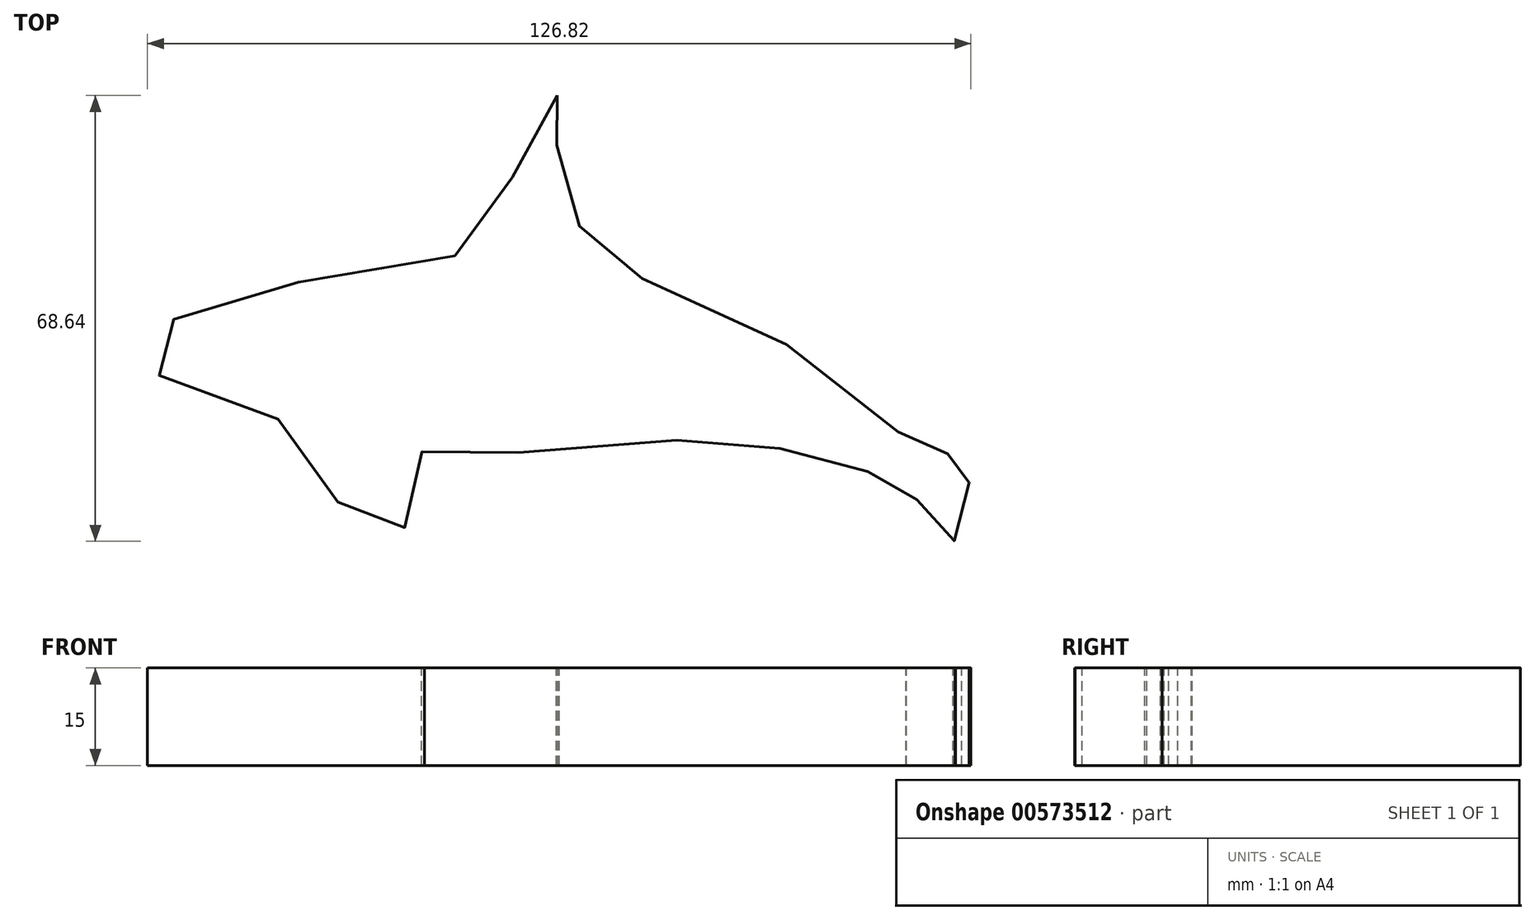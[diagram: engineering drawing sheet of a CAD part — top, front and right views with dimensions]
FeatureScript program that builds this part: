
annotation { "Feature Type Name" : "Feature", "Feature Type Description" : "" }
export const myFeature = defineFeature(function(context is Context, id is Id, definition is map)
    precondition{}
    {
        {
            var Q0;
            Q0=qCreatedBy(makeId("Top.planeOp"),FACE);
            var sketch = newSketch(context, id + "F0", { "sketchPlane" : qUnion([Q0])});
            skFitSpline(sketch, "E0", {"points": [v(3.98, 39.05) * mm, v(4.31, 38.75) * mm, v(4.31, 38.29) * mm, v(4.31, 37.62) * mm, v(4.31, 36.89) * mm, v(4.21, 36.2) * mm, v(4.21, 35.3) * mm, v(4.01, 34.13) * mm, v(3.91, 33.4) * mm, v(3.91, 32.53) * mm, v(3.91, 31.53) * mm, v(3.91, 30.36) * mm, v(4.21, 29) * mm, v(4.58, 27.67) * mm, v(5.04, 26.33) * mm, v(6.58, 22.13) * mm, v(7.05, 20.08) * mm, v(7.92, 17.44) * mm, v(8.51, 15.91) * mm, v(9.21, 14.92) * mm, v(9.62, 14.5) * mm, v(11.27, 13.4) * mm, v(13.61, 12.34) * mm, v(18.48, 10.29) * mm, v(26.57, 7.18) * mm, v(34.07, 3.73) * mm, v(39.5, 0.6) * mm, v(46.48, -3.74) * mm, v(51.83, -7.55) * mm, v(55.4, -10.93) * mm, v(57.17, -13.88) * mm, v(57.75, -14.94) * mm, v(57.72, -15.36) * mm, v(57.88, -15.6) * mm, v(58.08, -15.8) * mm, v(58.44, -16.22) * mm, v(58.83, -16.39) * mm, v(60.57, -16.39) * mm, v(62.4, -16.22) * mm, v(64.56, -16.16) * mm, v(65.78, -16.58) * mm, v(67.22, -17.16) * mm, v(67.66, -17.83) * mm, v(67.66, -18.21) * mm, v(67.42, -18.5) * mm, v(67.03, -18.8) * mm, v(66.53, -19.02) * mm, v(66.3, -19.27) * mm, v(67.06, -19.66) * mm, v(67.42, -20.46) * mm, v(67.42, -21.6) * mm, v(67.17, -22.76) * mm, v(66.78, -24.2) * mm, v(65, -27.35) * mm, v(64.96, -27.7) * mm, v(65.2, -28.09) * mm, v(65.28, -28.44) * mm, v(65.28, -28.96) * mm, v(65.28, -29.45) * mm, v(64.82, -29.52) * mm, v(64.3, -29.56) * mm, v(63.85, -29.56) * mm, v(63.36, -29.24) * mm, v(62.73, -28.9) * mm, v(62.24, -28.5) * mm, v(61.89, -27.67) * mm, v(61.15, -26.17) * mm, v(60.17, -24.49) * mm, v(58.77, -22.42) * mm, v(57.27, -21.1) * mm, v(55.66, -19.8) * mm, v(54.96, -19.13) * mm, v(54.75, -18.93) * mm, v(54.37, -18.54) * mm, v(54.16, -18.47) * mm, v(54.09, -18.61) * mm, v(53.67, -18.79) * mm, v(52.62, -18.82) * mm, v(49.78, -18.68) * mm, v(47.2, -18.3) * mm, v(45.34, -17.67) * mm, v(42.34, -16.49) * mm, v(40.5, -15.94) * mm, v(38.1, -15.24) * mm, v(35.12, -14.54) * mm, v(31.56, -13.94) * mm, v(28.97, -13.76) * mm, v(25.59, -13.86) * mm, v(21.61, -14.04) * mm, v(17.46, -14.36) * mm, v(3.25, -15.84) * mm, v(-0.79, -15.84) * mm, v(-6.42, -16.16) * mm, v(-11.47, -16.03) * mm, v(-14.42, -15.7) * mm, v(-16.14, -15.45) * mm, v(-16.85, -15.13) * mm, v(-16.85, -15.58) * mm, v(-16.66, -17.88) * mm, v(-16.53, -20.7) * mm, v(-16.6, -23.32) * mm, v(-17.1, -24.6) * mm, v(-17.62, -25.3) * mm, v(-18.77, -26.84) * mm, v(-20.37, -28) * mm, v(-21.46, -28.44) * mm, v(-22.6, -28.32) * mm, v(-24.33, -27.87) * mm, v(-25.93, -27.36) * mm, v(-27.73, -25.88) * mm, v(-29.9, -23.32) * mm, v(-34.13, -17.56) * mm, v(-35.92, -14.1) * mm, v(-36.17, -11.55) * mm, v(-36.81, -11.61) * mm, v(-38.73, -10.84) * mm, v(-40.2, -10.46) * mm, v(-46.7, -8.18) * mm, v(-52.68, -5.99) * mm, v(-56.7, -4.4) * mm, v(-57.78, -3.62) * mm, v(-58.44, -2.61) * mm, v(-58.63, -2.09) * mm, v(-59.01, -1.75) * mm, v(-59.06, -0.99) * mm, v(-58.44, 0) * mm, v(-57.67, 1.35) * mm, v(-56.15, 3.64) * mm, v(-53.8, 5.4) * mm, v(-51.71, 6.17) * mm, v(-47.8, 6.98) * mm, v(-39.45, 9.13) * mm, v(-32.63, 11.23) * mm, v(-20.15, 13.37) * mm, v(-16.02, 13.9) * mm, v(-11.48, 14.44) * mm, v(-7.9, 15.34) * mm, v(-5.68, 17.37) * mm, v(-4.3, 20.54) * mm, v(-3.47, 23.95) * mm, v(-2.63, 27.84) * mm, v(-1.54, 31.67) * mm, v(0, 35.14) * mm, v(1.23, 37.06) * mm, v(2.46, 38.4) * mm, v(3.98, 39.05) * mm]});
            skSolve(sketch);
        }
        {
            var Q0;
            Q0=sQuery(id+"F0.wireOp",EDGE,"E0");
            extrude(context, id + "F1", {"bodyType" : ToolBodyType.SURFACE, "surfaceEntities" : qUnion([Q0]), "depth" : 15 * mm, "offsetDistance" : 25 * mm});
        }
    });
